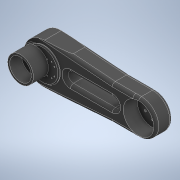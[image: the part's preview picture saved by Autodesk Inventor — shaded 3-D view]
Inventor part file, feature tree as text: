
AUTODESK INVENTOR PART (.ipt)
format: ipt  version: 2021 (Build 250183000, 183)  size: 468,992 bytes
history: native  units: mm
features: sketch x10, extrude x10, fillet x4, hole x3, pattern_circular x1
ambient origin geometry x8: Origin, YZ Plane, XZ Plane, XY Plane, X Axis, Y Axis, Z Axis, Center Point
bodies: Body1 (feature_tree)
feature tree (28):
  sketch  "Boceto1"  dims[d1=66.0mm d30=78.0mm]
  extrude  "Extrusión4"  Depth=78.0mm
  extrude  "Extrusión5"  Depth=6.0mm TaperAngle=0.0deg
  hole  "Agujero2"  [1 undecoded]
  pattern_circular  "Patrón circular2"  Count=6 Angle=360.0deg
  sketch  "Boceto4"  dims[d72=40.0mm d73=16.0mm]
  fillet  "Empalme5"  Radius=50.0mm
  fillet  "Empalme6"  Radius=50.0mm
  hole  "Agujero5"  [1 undecoded]
  extrude  "Extrusión9"  Depth=50.0mm
  sketch  "Boceto8"  dims[d85=50.0mm d86=32.0mm d87=12.0mm d88=11.65mm d89=10.5mm d90=7.0mm d91=21.0mm d92=2.8mm d93=4.4mm d94=5.6mm d95=4.4mm d96=0.8mm d97=0.8mm d98=0.8mm d99=0.8mm d100=0.8mm d101=0.8mm d102=2.0mm d103=2.0mm d104=2.0mm d105=2.0mm d106=2.0mm d107=2.0mm d108=2.0mm d109=2.0mm d110=2.0mm d111=2.0mm d136=50.0mm d137=50.0mm]
  extrude  "Extrusión10"  Depth=10.0mm
  extrude  "Extrusión11"  Depth=2.0mm
  sketch  "Boceto9"  dims[d149=6.0mm d187=20.0mm]
  extrude  "Extrusión13"  Depth=2.0mm
  extrude  "Extrusión14"  Depth=2.0mm
  extrude  "Extrusión15"  Depth=2.0mm
  hole  "Agujero6"  [1 undecoded]
  extrude  "Extrusión16"  Depth=2.0mm
  extrude  "Extrusión17"  Depth=2.0mm TaperAngle=360.0deg
  fillet  "Empalme7"  Radius=62.0mm
  fillet  "Empalme8"  Radius=3.0mm
  sketch  "Boceto3"  dims[d38=33.0mm d39=0.0mm d40=6.0mm d41=0.0mm]
  sketch  "Boceto6"  dims[d74=3.0mm]
  sketch  "Boceto7"  dims[d75=3.958734mm d76=9.0mm d77=4.0mm d78=2.0mm d79=90.0deg d80=11.8mm d81=0.0mm d82=60.0mm d83=360.0deg]
  sketch  "Boceto10"  dims[d188=50.0mm d189=50.0mm]
  sketch  "Boceto11"  dims[d191=6.0mm d192=10.0mm]
  sketch  "Boceto12"  dims[d193=10.0mm d194=33.0mm d195=80.0mm d196=70.0mm d197=32.0mm d198=45.0deg d199=3.0mm d200=40.0mm d202=360.0deg d204=3.688101mm d205=9.0mm d206=4.0mm d207=2.0mm d208=90.0deg d209=10.0mm d210=0.0mm d213=62.0mm d214=3.0mm d215=0.0mm d216=32.0mm d217=50.0mm d218=23.0mm d219=11.5mm d220=2.2mm d221=2.2mm d222=2.2mm d223=2.2mm d224=2.2mm d225=2.2mm d226=2.2mm d227=2.2mm d228=2.2mm d229=2.2mm d230=27.0mm d231=16.0mm d232=8.0mm d233=13.5mm d234=13.5mm d235=8.0mm d236=8.0mm d237=8.0mm d238=8.0mm d239=8.0mm d240=8.0mm d241=6.0mm d242=8.307mm d243=22.006mm d244=1.042mm d245=1.042mm d246=11.2mm d247=0.8mm d248=0.8mm d249=0.8mm d250=0.8mm d251=1.75mm d252=0.8mm d253=1.75mm d254=0.8mm d255=3.0mm d256=0.0mm d257=2.2mm d258=0.0mm d262=49.235mm d263=3.0mm d264=0.0mm d265=28.934mm d266=0.0mm d267=13.736mm d268=22.934mm d269=0.0mm d270=2.013mm d271=5.0mm d272=4.0mm d273=2.0mm d274=90.0deg d275=7.6mm d276=20.594885mm d277=6.0mm d278=0.0mm d282=62.0mm d283=3.0mm d284=0.0mm d285=2.0mm d286=2.0mm d53=0.5mm d54=0.872665mm d55=0.5mm d56=0.872665mm]
note: 3 required parameter values undecoded (feature->parameter linkage not recoverable at this tier; creation-order binding heuristic only, values carry confidence <= 0.55)
